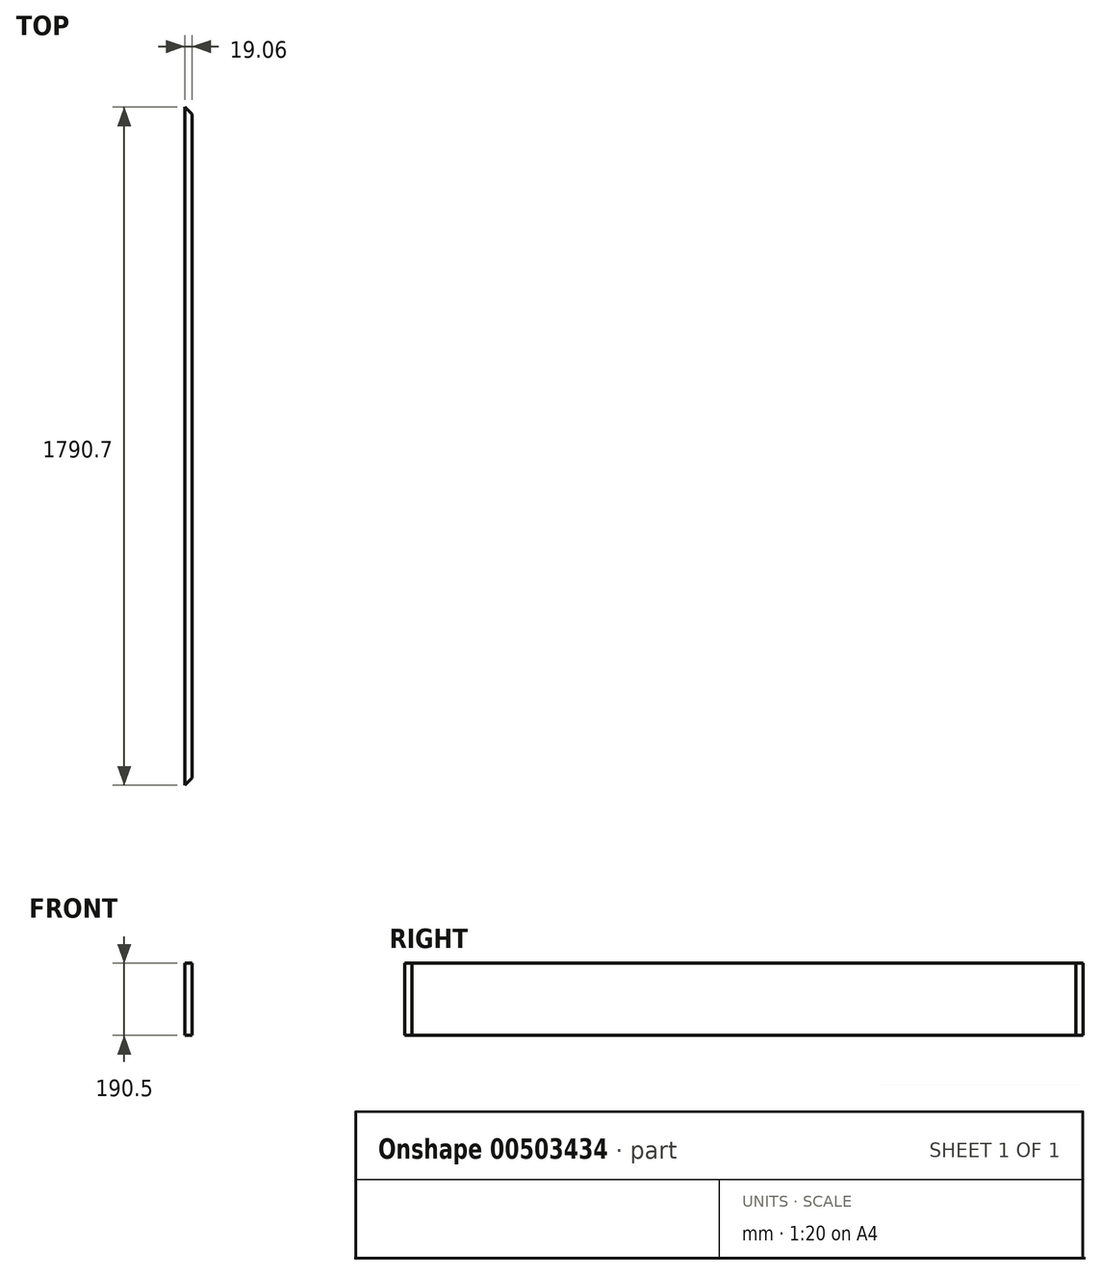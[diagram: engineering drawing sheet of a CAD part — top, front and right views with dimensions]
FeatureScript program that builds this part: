
annotation { "Feature Type Name" : "Feature", "Feature Type Description" : "" }
export const myFeature = defineFeature(function(context is Context, id is Id, definition is map)
    precondition{}
    {
        {
            var Q0;
            Q0=qCreatedBy(makeId("Front.planeOp"),FACE);
            var sketch = newSketch(context, id + "F0", { "sketchPlane" : qUnion([Q0])});
            skLineSegment(sketch, "E0", {"start": v(0, 68.06) * mm, "end": v(0, -58.62) * mm, "construction": true});
            skLineSegment(sketch, "E1", {"start": v(-60.84, 0) * mm, "end": v(61.95, 0) * mm, "construction": true});
            skLineSegment(sketch, "E2.bottom", {"start": v(-9.53, -95.25) * mm, "end": v(9.52, -95.25) * mm});
            skLineSegment(sketch, "E2.top", {"start": v(-9.53, 95.25) * mm, "end": v(9.52, 95.25) * mm});
            skLineSegment(sketch, "E2.left", {"start": v(-9.53, -95.25) * mm, "end": v(-9.53, 95.25) * mm});
            skLineSegment(sketch, "E2.right", {"start": v(9.53, -95.25) * mm, "end": v(9.53, 95.25) * mm});
            skSolve(sketch);
        }
        {
            var Q0;
            Q0=makeQuery(id+"F0.imprint","IMPRINT",FACE,{"disambiguationData":[TD([[makeQuery(id+"F0.imprint","IMPRINT",EDGE,{"derivedFrom":sQuery(id+"F0.wireOp",EDGE,"E2.bottom")}),1.0]])]});
            extrude(context, id + "F1", {"entities" : qUnion([Q0]), "endBound" : BoundingType.SYMMETRIC, "depth" : 1828.8 * mm});
        }
        {
            var Q0;
            Q0=makeQuery(id+"F1.opExtrude","CAP_EDGE",EDGE,{"disambiguationData":[OSD([sQuery(id+"F0.wireOp",EDGE,"E2.right")])],"isStart":false});
            var Q1;
            Q1=makeQuery(id+"F1.opExtrude","CAP_EDGE",EDGE,{"disambiguationData":[OSD([sQuery(id+"F0.wireOp",EDGE,"E2.right")])],"isStart":true});
            chamfer(context, id + "F2", {"entities" : qUnion([Q0, Q1]), "width" : 38.1 * mm, "tangentPropagation" : true});
        }
    });
